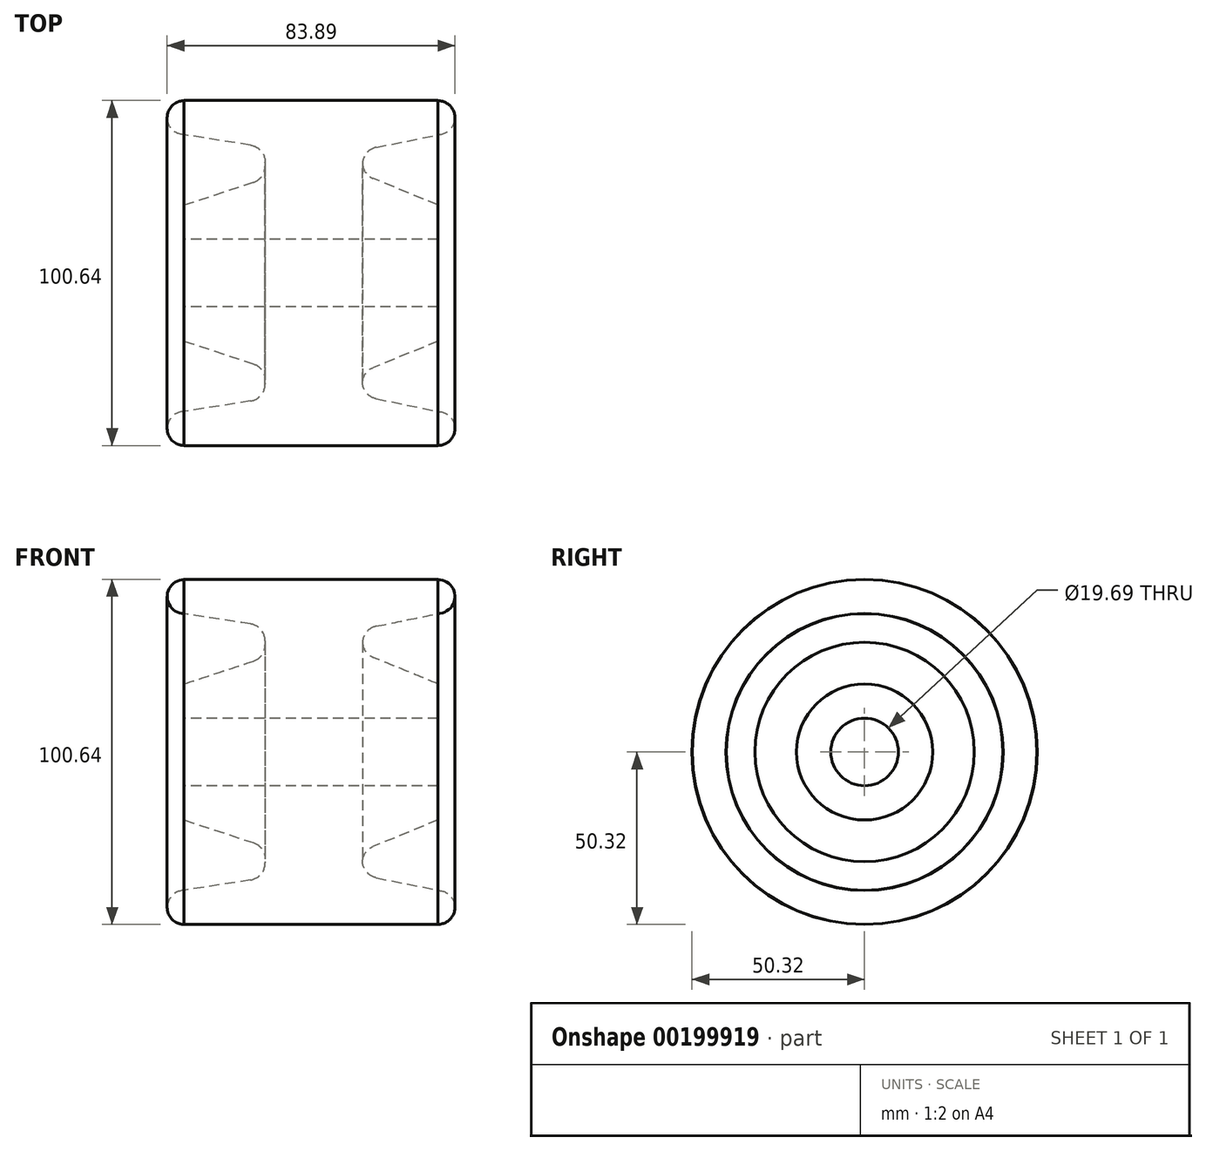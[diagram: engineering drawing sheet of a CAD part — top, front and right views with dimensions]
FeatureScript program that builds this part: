
annotation { "Feature Type Name" : "Feature", "Feature Type Description" : "" }
export const myFeature = defineFeature(function(context is Context, id is Id, definition is map)
    precondition{}
    {
        {
            var Q0;
            Q0=qCreatedBy(makeId("Top.planeOp"),FACE);
            var sketch = newSketch(context, id + "F0", { "sketchPlane" : qUnion([Q0])});
            skLineSegment(sketch, "E0", {"start": v(-43.9, 0) * mm, "end": v(48.46, 0) * mm, "construction": true});
            skLineSegment(sketch, "E1", {"start": v(-31.98, -9.84) * mm, "end": v(42.02, -9.84) * mm});
            skLineSegment(sketch, "E2", {"start": v(42.02, -9.84) * mm, "end": v(5.02, -9.84) * mm});
            skLineSegment(sketch, "E3", {"start": v(5.02, -9.84) * mm, "end": v(5.02, -50.32) * mm});
            skLineSegment(sketch, "E4", {"start": v(5.02, -50.32) * mm, "end": v(42.02, -50.32) * mm});
            skLineSegment(sketch, "E5", {"start": v(42.02, -50.32) * mm, "end": v(42.02, -40.32) * mm});
            skLineSegment(sketch, "E6", {"start": v(42.02, -40.32) * mm, "end": v(24.01, -36.66) * mm});
            skLineSegment(sketch, "E7", {"start": v(20, -32.21) * mm, "end": v(20, -31.76) * mm});
            skLineSegment(sketch, "E8", {"start": v(23.12, -27.58) * mm, "end": v(42.02, -19.84) * mm});
            skLineSegment(sketch, "E9", {"start": v(42.02, -19.84) * mm, "end": v(42.02, -9.84) * mm});
            skPoint(sketch, "E10.visualSharp", {"position": v(20, -28.86) * mm});
            skArc(sketch, "E10.filletArc", {"start": v(23.12, -27.58) * mm, "mid": v(20.86, -29.43) * mm, "end": v(20, -32.21) * mm});
            skPoint(sketch, "E11.visualSharp", {"position": v(20, -35.85) * mm});
            skArc(sketch, "E11.filletArc", {"start": v(20, -31.76) * mm, "mid": v(21.14, -34.93) * mm, "end": v(24.01, -36.66) * mm});
            skCircle(sketch, "E12", {"center": v(42.02, -45.32) * mm, "radius": 4.94 * mm});
            skLineSegment(sketch, "E13", {"start": v(5.02, -50.32) * mm, "end": v(-31.98, -50.32) * mm});
            skLineSegment(sketch, "E14", {"start": v(-31.98, -50.32) * mm, "end": v(-31.98, -40.32) * mm});
            skLineSegment(sketch, "E15", {"start": v(-31.98, -40.32) * mm, "end": v(-12.61, -37.32) * mm});
            skLineSegment(sketch, "E16", {"start": v(-8.38, -32.38) * mm, "end": v(-8.38, -31.2) * mm});
            skLineSegment(sketch, "E17", {"start": v(-11.82, -26.46) * mm, "end": v(-31.98, -19.84) * mm});
            skLineSegment(sketch, "E18", {"start": v(-31.98, -19.84) * mm, "end": v(-31.98, -9.84) * mm});
            skPoint(sketch, "E19.visualSharp", {"position": v(-8.38, -27.58) * mm});
            skArc(sketch, "E19.filletArc", {"start": v(-8.38, -31.2) * mm, "mid": v(-9.33, -28.27) * mm, "end": v(-11.82, -26.46) * mm});
            skPoint(sketch, "E20.visualSharp", {"position": v(-8.38, -36.66) * mm});
            skArc(sketch, "E20.filletArc", {"start": v(-12.61, -37.32) * mm, "mid": v(-9.58, -35.63) * mm, "end": v(-8.38, -32.38) * mm});
            skCircle(sketch, "E21", {"center": v(-31.98, -45.32) * mm, "radius": 4.95 * mm});
            skSolve(sketch);
        }
        {
            var Q0;
            Q0 = qSketchRegion(id + "F0", true);
            var Q1;
            Q1=sQuery(id+"F0.wireOp",EDGE,"E0");
            revolve(context, id + "F1", {"entities" : qUnion([Q0]), "axis" : qUnion([Q1]), "revolveType" : RevolveType.FULL});
        }
    });
